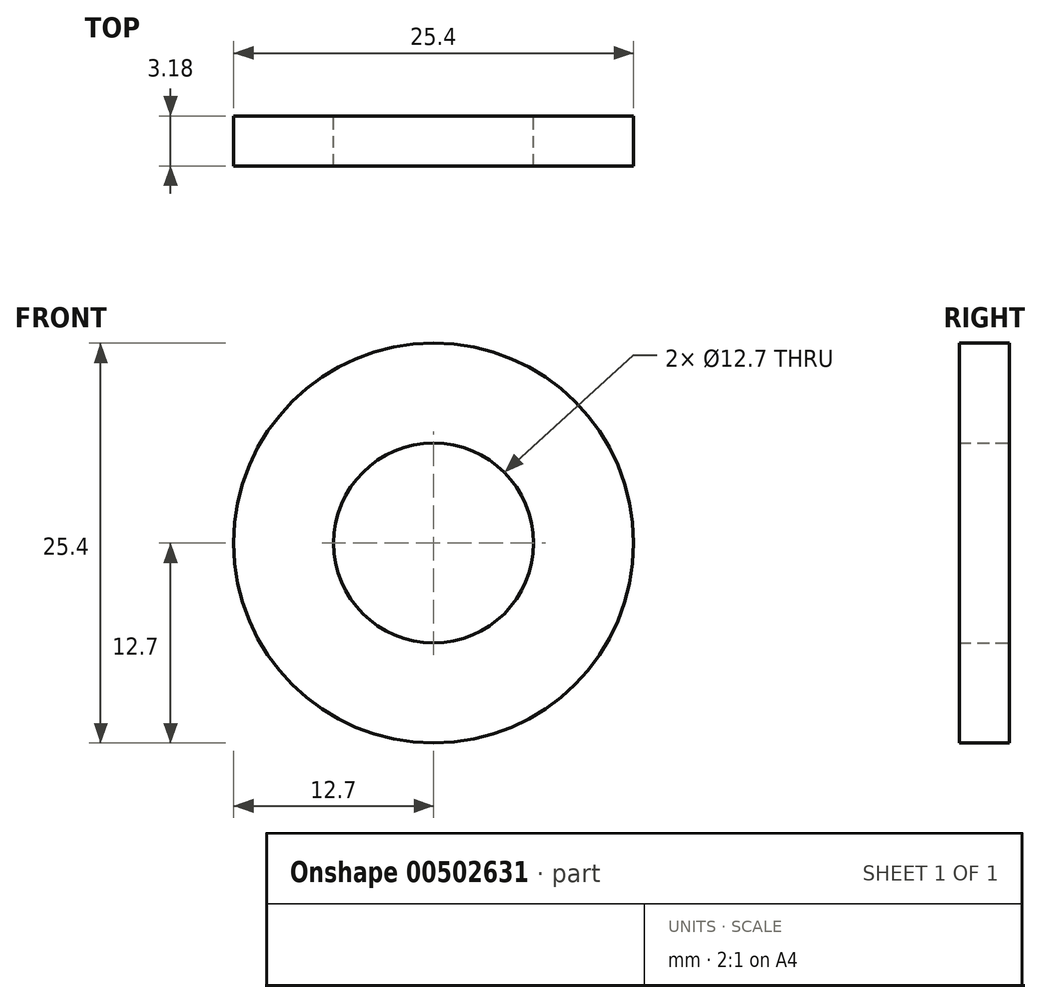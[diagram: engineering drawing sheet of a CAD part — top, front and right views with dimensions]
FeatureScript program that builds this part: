
annotation { "Feature Type Name" : "Feature", "Feature Type Description" : "" }
export const myFeature = defineFeature(function(context is Context, id is Id, definition is map)
    precondition{}
    {
        {
            var Q0;
            Q0=qCreatedBy(makeId("Front.planeOp"),FACE);
            var sketch = newSketch(context, id + "F0", { "sketchPlane" : qUnion([Q0])});
            skCircle(sketch, "E0", {"center": v(0, 0) * mm, "radius": 6.35 * mm});
            skCircle(sketch, "E1", {"center": v(0, 0) * mm, "radius": 12.7 * mm});
            skSolve(sketch);
        }
        {
            var Q0;
            Q0=makeQuery(id+"F0.imprint","IMPRINT",FACE,{"disambiguationData":[TD([[makeQuery(id+"F0.imprint","IMPRINT",EDGE,{"derivedFrom":sQuery(id+"F0.wireOp",EDGE,"E0")}),-1.0]])]});
            extrude(context, id + "F1", {"entities" : qUnion([Q0]), "depth" : 3.17 * mm});
        }
    });
